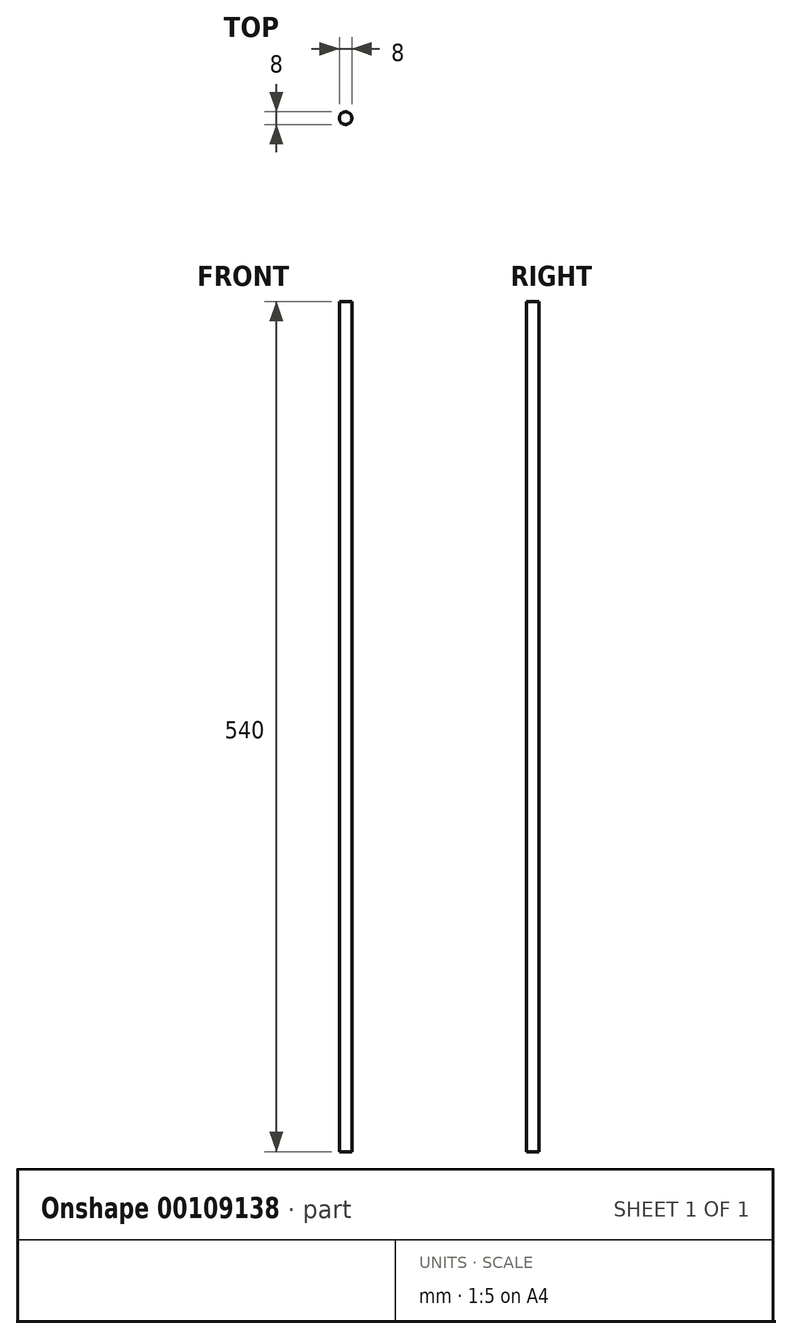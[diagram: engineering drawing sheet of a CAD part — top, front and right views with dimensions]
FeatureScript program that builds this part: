
annotation { "Feature Type Name" : "Feature", "Feature Type Description" : "" }
export const myFeature = defineFeature(function(context is Context, id is Id, definition is map)
    precondition{}
    {
        {
            var Q0;
            Q0=qCreatedBy(makeId("Top.planeOp"),FACE);
            var sketch = newSketch(context, id + "F0", { "sketchPlane" : qUnion([Q0])});
            skCircle(sketch, "E0", {"center": v(0, 0) * mm, "radius": 4 * mm});
            skSolve(sketch);
        }
        {
            var Q0;
            Q0=qSketchRegion(id+"F0",true);
            extrude(context, id + "F1", {"entities" : qUnion([Q0]), "depth" : 540 * mm});
        }
    });
